# Revit family: IS_TonicII_E3972_BIM_DE
name_source: partatom
category: Plumbing Fixtures
revit_build: Autodesk Revit MEP 2016 (Build: 20161004_0715(x64)
units: mm (PartAtom-declared; Revit-internal decimal feet)

## family parameters
Always vertical = No
Cut with Voids When Loaded = No
OmniClass Number = 23.45.05.14.21
OmniClass Title = Bathtubs
Part Type = Normal
Room Calculation Point = No
Round Connector Dimension = Use Diameter
Shared = No
Work Plane-Based = No

## types (2) — shared parameters
Accessories = www.idealstandard.de\ersatzteile
AssetType = Fixed
BIMobject category = Bath & Spas
BOSUseNativeGeometries = 1
Brand url = http://www.idealstandard.de
ConnectionType = Plumbing
CurrencyUnit = €
CurrentRevision = 1
DurationUnit = Jaar
EAN code = https://5017830487951
Edition number = 1
HasGrabHandles = No
IFC Classification = Sanitary Terminal
IfcExportAs = Sanitary terminal type
Installation instructions = http://www.idealstandard.de
LinearUnits = millimetres
MaintenanceInformation = www.idealstandard.de
Manufacturer = http://www.idealstandard.de
Manufacturer name = Ideal Standard
ManufacturerURL = http://www.idealstandard.de
Material main = Acrylic
NBS Reference Code = 35-06-08
NBS Reference Description = Baths
Nominal height = 490
Nominal width = 750
NominalHeight = 635 mm
NominalLength = 1695 mm  [stored 5.56102 ft]
NominalWidth = 745 mm  [stored 2.44423 ft]
OmniClass Code = 23-31 15 00
OmniClass Description = Bathtubs
Product Guid = 48067894-aeb2-4831-b78e-55bf6ab75e42
Product SKU = E3972
Product data url = https://bimobject.com
Product family = TONIC II
Product group = Bath Tub
Product name = TONIC II rectangular bath tub 1700x750mm
Product url = http://www.idealstandard.de
ProductInformation = www.idealstandard.de/produkte
QR code = http://bimobject.com
Space = Internal
SpareParts = www.idealstandard.de/ersatzteile
Technical description = http://www.idealstandard.de
URL = http://www.idealstandard.de
Uniclass 2.0 Code = PR-35-06-08
Uniclass 2.0 Description = Baths
Uniclass 2015 Code = Pr_40_20_06_08
Uniclass 2015 Name = Baths
Uniclass2015Code = Pr_40_20_06_08
Uniclass2015Title = Baths
Uniclass2015Version = Products v1.1
VolumeUnits = Litres
Weight Net (Kg) = 27.4
zero-valued in all types: Cost, DrainSize, MaterialThickness

## per-type parameters (varying)
| type | BIMObjectName | BarCode | Brand | CodePerformance | Color | Description | ExpectedLife | Features | Finish | IfcExportType | InstallationInstructions | MainColor | Material | Model | ModelNumber | ModelReference | Name | NettWeight | Product certification | Shape | Size |
| Default | ISI_IdealStandard_Baths |  |  |  |  |  |  |  |  |  |  |  |  |  |  |  | ISI_IdealStandard_Baths |  |  |  |  |
| E397201 TONIC II rectangular bath tub 1700x750mm | ISI_IdealStandard_Baths_TONICII_E397201 | 5017830487951 | Ideal Standard | DIN EN 14516, DIN EN 232, DIN EN | White | E397201 TONIC II rectangular bath tub 1700x750mm | 25 | TONIC II rectangular bath tub 1700x750mm | White | BATH | www.idealstandard.de\produkte | White | Sanitary Brass | E397201 | E397201 | E397201 TONIC II rectangular bath tub 1700x750mm | ISI_IdealStandard_Baths_TONICII_E397201 | 27,4 kg | DIN EN 14516, DIN EN 232, DIN EN | Rectangular | 1695x745x635 mm |

note: [stored X ft] marks values corroborated as IEEE doubles in the binary element streams (Revit-internal decimal feet)

## geometry (parser evidence)
native form markers: Blend x2, Sweep x2
no freeform markers — native parametric forms only
